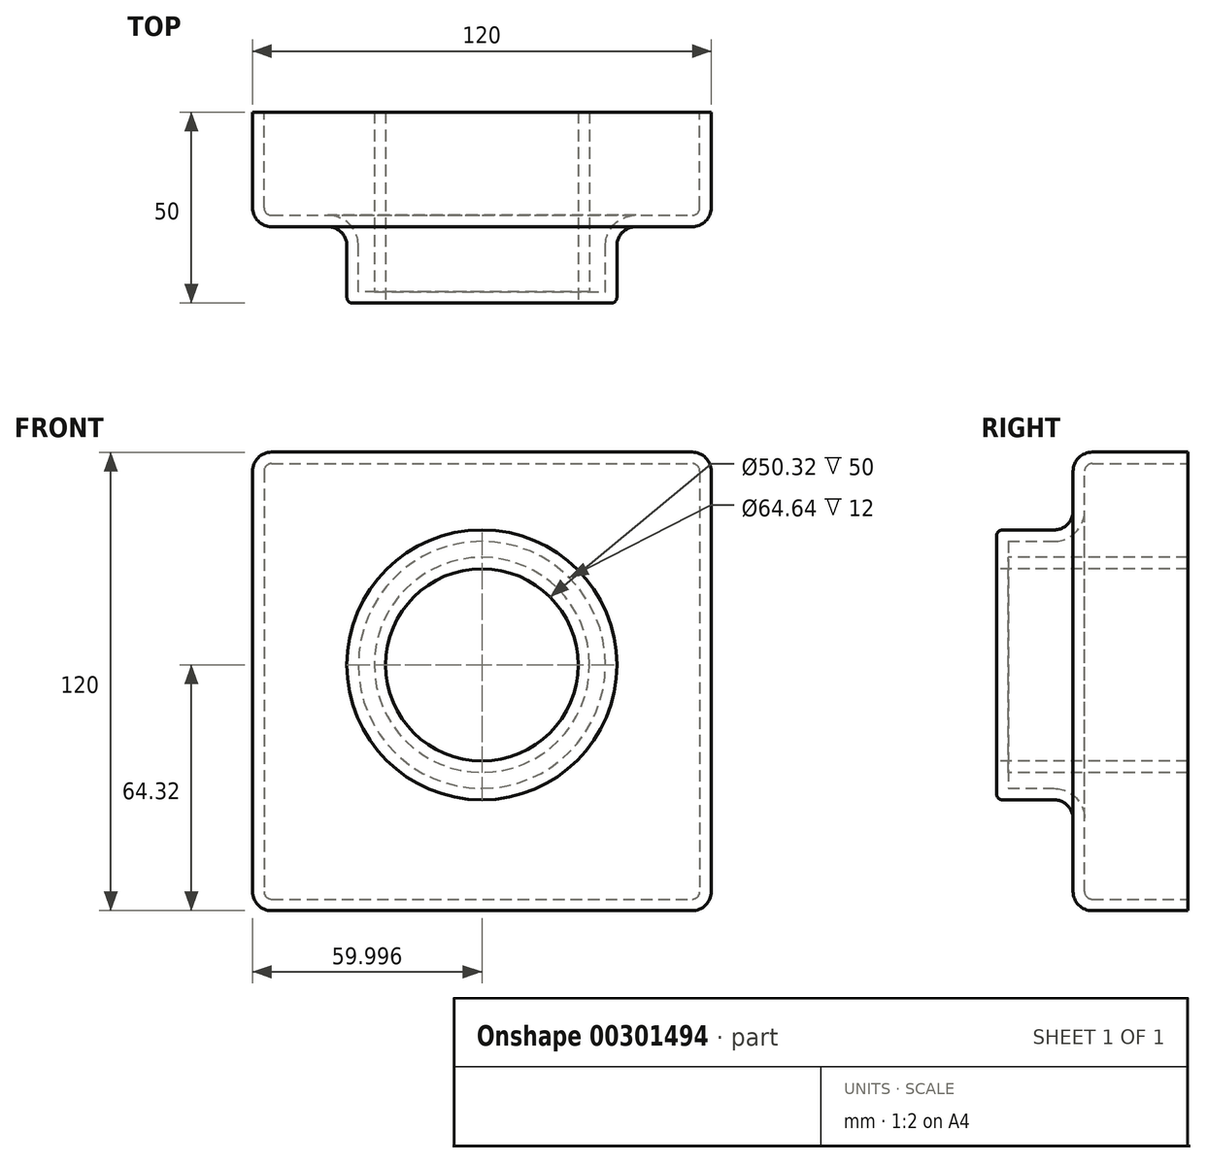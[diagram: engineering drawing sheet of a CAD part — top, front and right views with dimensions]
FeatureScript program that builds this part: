
annotation { "Feature Type Name" : "Feature", "Feature Type Description" : "" }
export const myFeature = defineFeature(function(context is Context, id is Id, definition is map)
    precondition{}
    {
        {
            var Q0;
            Q0=qCreatedBy(makeId("Front.planeOp"),FACE);
            var sketch = newSketch(context, id + "F0", { "sketchPlane" : qUnion([Q0])});
            skLineSegment(sketch, "E0.bottom", {"start": v(-30.72, 55.68) * mm, "end": v(89.28, 55.68) * mm});
            skLineSegment(sketch, "E0.top", {"start": v(-30.72, -64.32) * mm, "end": v(89.28, -64.32) * mm});
            skLineSegment(sketch, "E0.left", {"start": v(-30.72, 55.68) * mm, "end": v(-30.72, -64.32) * mm});
            skLineSegment(sketch, "E0.right", {"start": v(89.28, 55.68) * mm, "end": v(89.28, -64.32) * mm});
            skSolve(sketch);
        }
        {
            var Q0;
            Q0=makeQuery(id+"F0.imprint","IMPRINT",FACE,{"disambiguationData":[TD([[makeQuery(id+"F0.imprint","IMPRINT",EDGE,{"derivedFrom":sQuery(id+"F0.wireOp",EDGE,"E0.bottom")}),-1.0]])]});
            extrude(context, id + "F1", {"entities" : qUnion([Q0]), "depth" : 30 * mm});
        }
        {
            var Q0;
            Q0=makeQuery(id+"F1.opExtrude","CAP_FACE",FACE,{"disambiguationData":[OSD([sQuery(id+"F0.wireOp",EDGE,"E0.bottom"),sQuery(id+"F0.wireOp",EDGE,"E0.top"),sQuery(id+"F0.wireOp",EDGE,"E0.left"),sQuery(id+"F0.wireOp",EDGE,"E0.right")])],"isStart":false});
            var sketch = newSketch(context, id + "F2", { "sketchPlane" : qUnion([Q0])});
            skCircle(sketch, "E1", {"center": v(29.28, 0) * mm, "radius": 35.32 * mm});
            skPoint(sketch, "E1.centerSnap0", {"position": v(29.28, 55.68) * mm});
            skSolve(sketch);
        }
        {
            var Q0;
            Q0=makeQuery(id+"F2.imprint","IMPRINT",FACE,{"disambiguationData":[TD([[makeQuery(id+"F2.imprint","IMPRINT",EDGE,{"derivedFrom":sQuery(id+"F2.wireOp",EDGE,"E1")}),1.0]])]});
            extrude(context, id + "F3", {"entities" : qUnion([Q0]), "operationType" : NewBodyOperationType.ADD, "depth" : 20 * mm});
        }
        {
            var Q0;
            Q0=makeQuery(id+"F3.opExtrude","CAP_FACE",FACE,{"disambiguationData":[OSD([sQuery(id+"F2.wireOp",EDGE,"E1")])],"isStart":false});
            var sketch = newSketch(context, id + "F4", { "sketchPlane" : qUnion([Q0])});
            skCircle(sketch, "E2", {"center": v(29.28, 0) * mm, "radius": 25.16 * mm});
            skSolve(sketch);
        }
        {
            var Q0;
            Q0=makeQuery(id+"F4.imprint","IMPRINT",FACE,{"disambiguationData":[TD([[makeQuery(id+"F4.imprint","IMPRINT",EDGE,{"derivedFrom":sQuery(id+"F4.wireOp",EDGE,"E2")}),1.0]])]});
            extrude(context, id + "F5", {"entities" : qUnion([Q0]), "operationType" : NewBodyOperationType.REMOVE, "oppositeDirection" : true, "depth" : 106.93 * mm});
        }
        {
            var Q0;
            Q0=makeQuery(id+"F1.opExtrude","CAP_FACE",FACE,{"disambiguationData":[OSD([sQuery(id+"F0.wireOp",EDGE,"E0.bottom"),sQuery(id+"F0.wireOp",EDGE,"E0.top"),sQuery(id+"F0.wireOp",EDGE,"E0.left"),sQuery(id+"F0.wireOp",EDGE,"E0.right")])],"isStart":false});
            var Q1;
            Q1=makeQuery(id+"F1.opExtrude","SWEPT_EDGE",EDGE,{"disambiguationData":[OSD([sQuery(id+"F0.wireOp",EDGE,"E0.bottom"),sQuery(id+"F0.wireOp",EDGE,"E0.left")])]});
            var Q2;
            Q2=makeQuery(id+"F1.opExtrude","SWEPT_EDGE",EDGE,{"disambiguationData":[OSD([sQuery(id+"F0.wireOp",EDGE,"E0.bottom"),sQuery(id+"F0.wireOp",EDGE,"E0.right")])]});
            var Q3;
            Q3=makeQuery(id+"F1.opExtrude","SWEPT_EDGE",EDGE,{"disambiguationData":[OSD([sQuery(id+"F0.wireOp",EDGE,"E0.top"),sQuery(id+"F0.wireOp",EDGE,"E0.right")])]});
            var Q4;
            Q4=makeQuery(id+"F1.opExtrude","CAP_EDGE",EDGE,{"disambiguationData":[OSD([sQuery(id+"F0.wireOp",EDGE,"E0.top")])],"isStart":false});
            var Q5;
            Q5=makeQuery(id+"F1.opExtrude","SWEPT_EDGE",EDGE,{"disambiguationData":[OSD([sQuery(id+"F0.wireOp",EDGE,"E0.top"),sQuery(id+"F0.wireOp",EDGE,"E0.left")])]});
            fillet(context, id + "F6", {"entities" : qUnion([Q0, Q1, Q2, Q3, Q4, Q5]), "radius" : 5 * mm, "tangentPropagation" : true, "allowEdgeOverflow" : false});
        }
        {
            var Q0;
            Q0=makeQuery(id+"F3.opExtrude","CAP_EDGE",EDGE,{"disambiguationData":[OSD([sQuery(id+"F2.wireOp",EDGE,"E1")])],"isStart":false});
            fillet(context, id + "F7", {"entities" : qUnion([Q0]), "radius" : 1.5 * mm, "tangentPropagation" : true, "allowEdgeOverflow" : false});
        }
        {
            var Q0;
            Q0=makeQuery(id+"F1.opExtrude","CAP_FACE",FACE,{"disambiguationData":[OSD([sQuery(id+"F0.wireOp",EDGE,"E0.bottom"),sQuery(id+"F0.wireOp",EDGE,"E0.top"),sQuery(id+"F0.wireOp",EDGE,"E0.left"),sQuery(id+"F0.wireOp",EDGE,"E0.right")])],"isStart":true});
            shell(context, id + "F8", {"entities" : qUnion([Q0]), "thickness" : 3 * mm});
        }
    });
